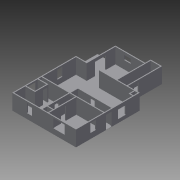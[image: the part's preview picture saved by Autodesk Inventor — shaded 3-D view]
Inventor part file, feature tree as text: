
AUTODESK INVENTOR PART (.ipt)
format: ipt  version: 2013 SP2 (Build 170200200, 200)  size: 483,840 bytes
history: native  units: in
note: dims shown in document units (in); Inventor stores cm internally (conversion verified against a paired STEP export)
features: extrude x10, sketch x7, projected_geometry x6
ambient origin geometry x8: Origin, YZ Plane, XZ Plane, XY Plane, X Axis, Y Axis, Z Axis, Center Point
bodies: Solid1 (feature_tree)
feature tree (23):
  sketch  "Sketch1"  dims[d0=392.0in d2=392.0in d4=210.0in]
  extrude  "Extrusion1"  Depth=210.0in
  extrude  "Extrusion2"  Depth=70.0in
  extrude  "Extrusion3"  Depth=43.0in
  sketch  "Sketch2"  dims[d6=34.0in d7=70.0in d8=73.0in d9=183.0in]
  extrude  "Extrusion4"  Depth=61.0in
  extrude  "Extrusion5"  Depth=210.0in
  extrude  "Extrusion6"  Depth=6.0in
  extrude  "Extrusion7"  Depth=6.0in
  extrude  "Extrusion8"  Depth=6.0in
  extrude  "Extrusion9"  Depth=6.0in
  extrude  "Extrusion10"  Depth=6.0in
  projected_geometry  "Projected Loop1"
  projected_geometry  "Projected Loop2"
  projected_geometry  "Projected Loop3"
  sketch  "Sketch3"  dims[d10=34.0in d11=43.0in]
  sketch  "Sketch4"  dims[d12=170.0in d13=61.0in]
  sketch  "Sketch5"  dims[d14=392.0in d15=210.0in]
  projected_geometry  "Projected Loop4"
  sketch  "Sketch6"  dims[d16=6.0in d17=6.0in d18=6.0in d19=6.0in d20=6.0in]
  sketch  "Sketch7"  dims[d21=6.0in d22=6.0in d24=6.0in d25=6.0in d26=6.0in d27=6.0in d28=6.0in d29=6.0in d30=6.0in d31=6.0in d32=6.0in d34=6.0in d35=6.0in d37=68.0in d38=117.0in d45=34.0in d46=44.0in d47=6.0in d48=174.0in d49=6.0in d50=28.0in d51=6.0in d52=74.0in d53=30.0in d54=6.0in d55=54.0in d56=27.0in d57=39.0in d58=34.0in d59=6.0in d60=392.0in d61=103.0in d62=30.0in d63=168.0in d64=24.0in d65=33.0in d66=6.0in d67=144.0in d68=29.0in d69=73.0in d70=70.0in d71=68.0in d72=58.0in d73=75.0in d74=94.0in d75=0.0in d76=1.0in d77=0.0in d78=1.0in d79=0.0in d80=18.0in d81=0.0in d82=14.0in d83=0.0in d84=90.0in d85=31.0in d86=31.0in d87=9.0in d88=69.0in d89=70.0in d90=31.0in d91=9.0in d92=23.0in d93=0.0in d94=89.0in d95=34.0in d96=31.0in d97=9.0in d98=86.0in d99=47.0in d100=23.0in d101=20.0in d102=23.0in d103=0.0in d104=41.0in d106=59.0in d107=50.0in d108=17.0in d109=23.0in d110=0.0in d111=271.0in d112=31.0in d113=31.0in d114=9.0in d115=31.0in d116=9.0in d117=59.0in d118=80.0in d119=23.0in d120=0.0in d121=1.0in d122=0.0in]
  projected_geometry  "Projected Loop5"
  projected_geometry  "Projected Loop6"
